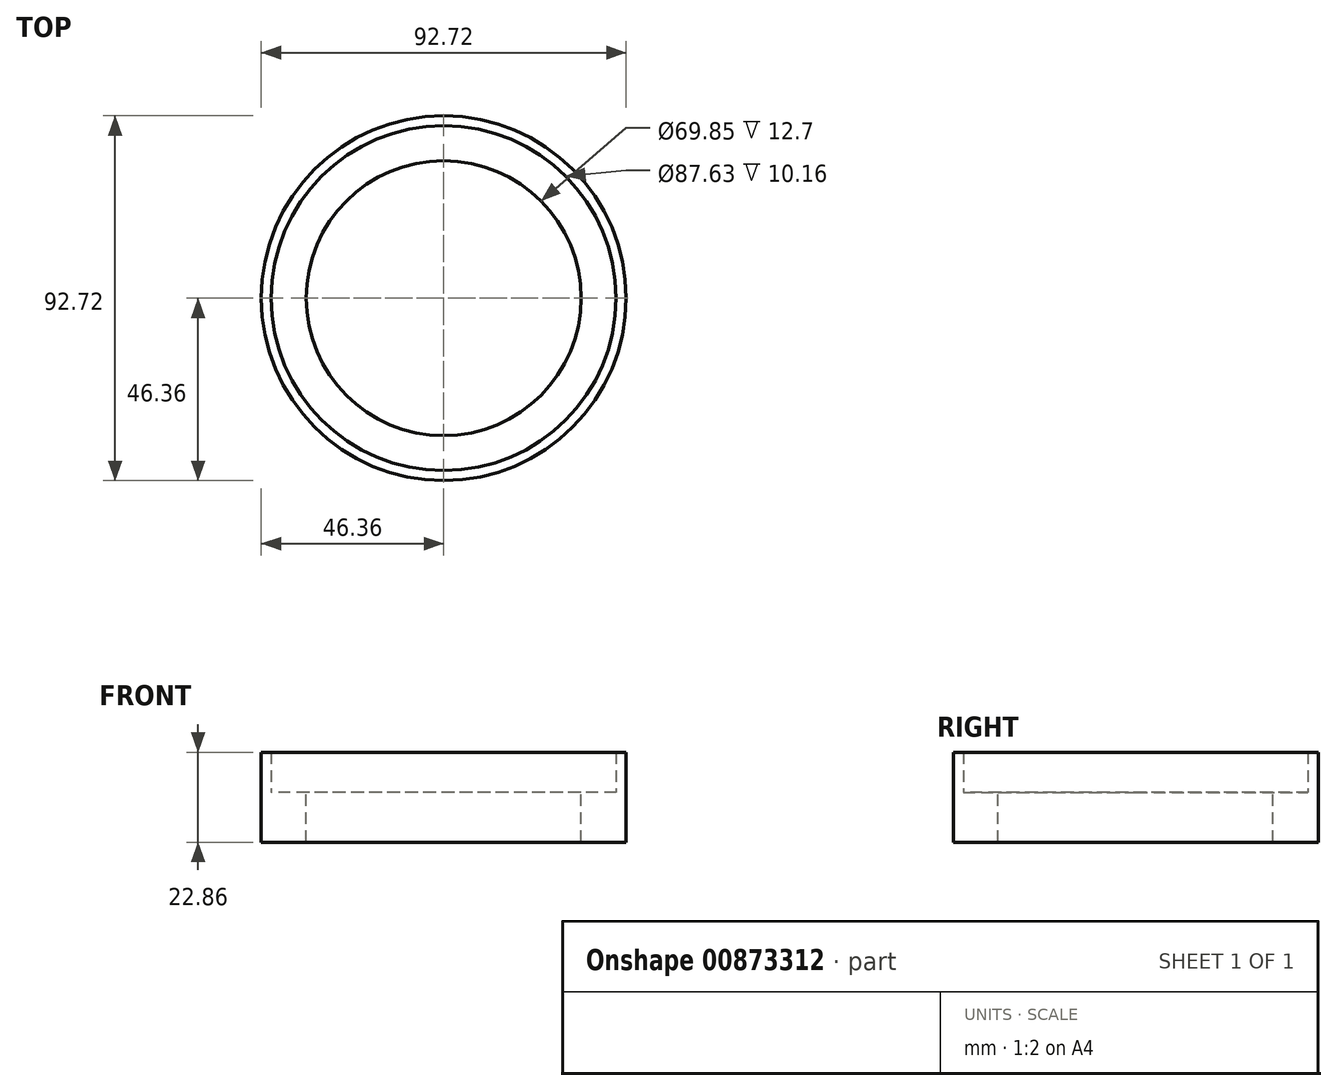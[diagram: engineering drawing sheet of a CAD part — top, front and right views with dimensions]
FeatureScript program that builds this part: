
annotation { "Feature Type Name" : "Feature", "Feature Type Description" : "" }
export const myFeature = defineFeature(function(context is Context, id is Id, definition is map)
    precondition{}
    {
        {
            var Q0;
            Q0=qCreatedBy(makeId("Top.planeOp"),FACE);
            var sketch = newSketch(context, id + "F0", { "sketchPlane" : qUnion([Q0])});
            skCircle(sketch, "E0", {"center": v(0, 0) * mm, "radius": 43.82 * mm});
            skCircle(sketch, "E1", {"center": v(0, 0) * mm, "radius": 46.35 * mm});
            skCircle(sketch, "E2", {"center": v(0, 0) * mm, "radius": 34.93 * mm});
            skSolve(sketch);
        }
        {
            var Q0;
            Q0 = qSketchRegion(id + "F0", true);
            var Q1;
            Q1=makeQuery(id+"F0.imprint","IMPRINT",FACE,{"disambiguationData":[TD([[makeQuery(id+"F0.imprint","IMPRINT",EDGE,{"derivedFrom":sQuery(id+"F0.wireOp",EDGE,"E0")}),1.0]])]});
            extrude(context, id + "F1", {"entities" : qUnion([Q0, Q1]), "depth" : -12.7 * mm, "offsetDistance" : 25.4 * mm});
        }
        {
            var Q0;
            Q0=makeQuery(id+"F0.imprint","IMPRINT",FACE,{"disambiguationData":[TD([[makeQuery(id+"F0.imprint","IMPRINT",EDGE,{"derivedFrom":sQuery(id+"F0.wireOp",EDGE,"E0")}),-1.0]])]});
            extrude(context, id + "F2", {"entities" : qUnion([Q0]), "operationType" : NewBodyOperationType.ADD, "depth" : 10.16 * mm, "offsetDistance" : 25.4 * mm});
        }
    });
